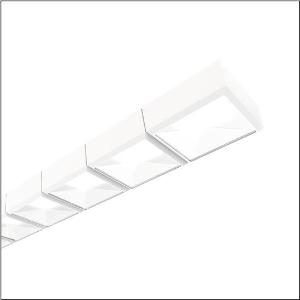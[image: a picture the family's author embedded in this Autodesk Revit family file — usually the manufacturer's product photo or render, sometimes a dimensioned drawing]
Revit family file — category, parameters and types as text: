
# Revit family: scriptus_r__11_5mz212d04wa_64be
name_source: partatom
category: Lighting Fixtures
units: mm (PartAtom-declared; Revit-internal decimal feet)

## family parameters
Cut with Voids When Loaded = No
Host = Face
Light Source = No
Part Type = Normal
Room Calculation Point = No
Round Connector Dimension = Use Diameter
Shared = No

## types (1)
- Scriptus® 11 (1 x LED 4000K / CRI = 80 (unbekannt), 2410 lm, 4000K)
    Apparent Load = 35 VA
    CIE Flux Codes = 82 95 99 100 100
    Color Rendering = 80
    Color Temperature = 4000K
    Default Elevation = 1800 mm
    Description = Scriptus® 11, office luminaire, primary optical cover: lenses, CAT 2 (L<= 3000cd/m²), light emission: direct distribution, primary light characteristic: symmetric, installation type: surface-mounted, LED, rated luminous flux: 4.810lm, luminous efficacy: 139lm/W, light colour: 840, colour temperature: 4000K, control gear: ECG DALI, with terminal, 5-pole, mains connection: 230V, AC, 50Hz, rated input power: 35W, housing, luminaire housing, of aluminium, traffic white (RAL 9016), length: 1.658mm, width: 114mm, height: 57mm, protection rating (complete): IP20, insulation class (complete): insulation class I (protective earthing), certification: CE, ENEC, VDE, protection symbol: F, permissible operating ambient temperature: 0..+35°C, standard: EN 50419, packaging unit: 1 piece
    Height = 57 mm
    Lamp = 1 x LED 4000K / CRI >= 80 (unbekannt)
    Lamp Light Flux = 2410 lm
    Lamp count = 1
    Length = 1658 mm
    Luminous efficacy = 139 lm/W
    Manufacturer = Siteco
    ModVariant = No
    Model = 5MZ212D04WA
    Mounting Place = Ceiling
    Mounting Type = Surface mounted
    Number of Poles = 1
    OnlyDefault = Yes
    Power Factor = 1
    Product Name = Scriptus® 11
    Product group = office luminaire | ceiling mounted
    ProductGroupID = 304
    Protection Class = Protection class I
    Protection Degree = IP 20
    RLX_Detail_Level = 1
    RLX_Emergency_Light_Flux = 0 lm
    RLX_Emergency_Type = 0
    RLX_Emergency_Type_DB = No
    RlxData = <blob elided: 29481 chars, md5=ec5f1af5>
    Socket = socket
    Standby Power = 0 W
    System Light Flux = 4820 lm
    System Power = 35 W
    Type Comments = Product without accessories
    Type Image = l_1004833.jpg
    URL = http://relux.com
    VarID = ---
    Voltage = 0 V
    Weight = 0.00 kg
    Width = 114 mm

## geometry (parser evidence)
native form markers: Blend x4, Sweep x12
no freeform markers — native parametric forms only
